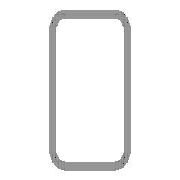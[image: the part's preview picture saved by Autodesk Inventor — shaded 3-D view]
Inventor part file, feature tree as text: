
AUTODESK INVENTOR PART (.ipt)
format: ipt  version: 2025.3 (Build 293356000, 356)  size: 150,016 bytes
history: native  units: mm (DEFAULTED — no unit token found)
features: other x4, plane x3, split x2, sketch x1
ambient origin geometry x8: Origin, YZ Plane, XZ Plane, XY Plane, X Axis, Y Axis, Z Axis, Center Point
bodies: Solid1 (feature_tree), Body (feature_tree)
feature tree (10):
  parser-record x1  (decoder bookkeeping rows leaked as tree rows — omitted from the tree; the rows remain in map.json)
  other  "Driven Length"
  other  "Start Plane"
  other  "End Plane"
  plane  "Work Plane4"
  split  "Split1"
  plane  "Work Plane5"
  split  "Split2"
  sketch  "Sketch3"  dims[d3=1042.584582mm d4=0.0mm d7=6.0mm d9=40.0mm d11=80.0mm d12=3.0mm d13=32.416264mm d14=1075.000846mm d15=20.0mm d16=40.0mm d17=90.0deg d18=1042.584582mm]
  plane  "Work Plane3"
